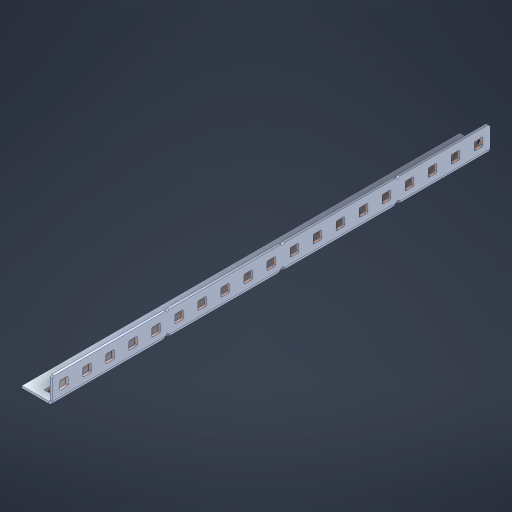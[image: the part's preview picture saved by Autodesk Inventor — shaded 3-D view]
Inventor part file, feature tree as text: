
AUTODESK INVENTOR PART (.ipt)
format: ipt  version: 2023 (Build 270158000, 158)  size: 732,672 bytes
history: native  units: in
note: dims shown in document units (in); Inventor stores cm internally (conversion verified against a paired STEP export)
features: other x43, extrude x37, sheet_metal_op x10, sketch x8, mirror x1, pattern_linear x1, chamfer x1
ambient origin geometry x8: Origin, YZ Plane, XZ Plane, XY Plane, X Axis, Y Axis, Z Axis, Center Point
bodies: Solid1 (feature_tree), Body (feature_tree)
feature tree (101):
  other  "Flange Pattern Plane"
  sheet_metal_op  "Flange Pattern"
  sheet_metal_op  "Body Pattern"
  other  "Arc Length"
  mirror  "Notch Mirror"
  pattern_linear  "Notch Pattern"  Spacing1=0.1875in  [1 undecoded]
  chamfer  "End Chamfer"
  extrude  "Half Cut"  Depth=0.0469in
  sketch  "Sketch1"  dims[d0=2.5in]
  other  "Plate1"
  sketch  "Sketch2"  dims[d1=9.5in]
  other  "Plate2"
  sheet_metal_op  "Bend1"
  sheet_metal_op  "Corner1"
  sketch  "Sketch3"  dims[d2=0.0469in]
  other  "Flange Pattern Sketch"
  sketch  "Sketch7"  dims[d3=0.0469in]
  other  "Srf1"
  other  "Srf2"
  sketch  "Sketch8"  dims[d4=0.0234in]
  sketch  "Sketch9"  dims[d5=0.0938in]
  other  "Srf91"
  sheet_metal_op  "Body Pattern Sketch"
  other  "Srf92"
  sketch  "Sketch13"  dims[d6=0.0469in]
  sketch  "Sketch14"  dims[d7=0.5in d8=90.0deg d9=0.0312in d10=0.1875in d11=0.0469in d12=0.0469in d16=0.182in d17=0.02in d18=0.0469in d19=0.0in d20=0.25in d21=0.25in d46=0.172in d47=1.0in d48=0.0in d49=0.182in d50=0.02in d51=0.25in d52=0.25in d53=0.0469in d54=0.0in d55=0.172in d56=1.0in d57=0.0in d60=7.4803in d62=0.5in d63=0.3937in d65=0.5in d85=0.1227in d86=0.1659in d88=0.04in d89=0.0469in d90=0.0in d91=0.04in d92=0.0491in d95=2.5in d96=0.04in d97=0.25in d98=45.0deg d101=0.0in d102=2.497in d131=0.5in d132=7.4803in d134=0.5in d139=0.5in]
  other  "Srf856"
  other  "Srf1310"
  other  "Srf1311"
  other  "Srf1312"
  other  "Srf1376"
  other  "Srf1377"
  other  "Srf1728"
  other  "Srf1755"
  other  "Srf1878"
  other  "Srf1879"
  other  "Srf1880"
  other  "Srf1881"
  other  "Srf1882"
  other  "Srf1883"
  other  "Srf1884"
  other  "Srf1885"
  other  "Srf1886"
  other  "Srf1887"
  other  "Srf1888"
  other  "Srf1889"
  other  "Srf1890"
  other  "Srf1942"
  other  "Srf1943"
  other  "Srf1944"
  other  "Srf1945"
  other  "Srf1946"
  other  "Srf1947"
  other  "Srf1948"
  other  "Srf1949"
  other  "Srf1950"
  other  "Srf1951"
  other  "Srf1952"
  other  "Srf1953"
  other  "Srf1954"
  sheet_metal_op  "Flange Stamp"
  sheet_metal_op  "Flange Circle"
  sheet_metal_op  "Body Stamp"
  sheet_metal_op  "Body Circle"
  sheet_metal_op  "Notch"
  extrude  "ExtrusionSrf2"  Depth=0.0469in
  extrude  "ExtrusionSrf92"  Depth=0.5in
  extrude  "ExtrusionSrf856"  Depth=0.02in
  extrude  "ExtrusionSrf1310"  Depth=0.0469in
  extrude  "ExtrusionSrf1311"  TaperAngle=0.0deg  [1 undecoded]
  extrude  "ExtrusionSrf1312"  Depth=0.5in
  extrude  "ExtrusionSrf1376"  Depth=0.5in
  extrude  "ExtrusionSrf1377"  Depth=0.5in
  extrude  "ExtrusionSrf1728"  Depth=0.5in TaperAngle=0.0deg
  extrude  "ExtrusionSrf1755"  Depth=0.5in
  extrude  "ExtrusionSrf1878"  Depth=0.02in
  extrude  "ExtrusionSrf1879"  Depth=0.5in
  extrude  "ExtrusionSrf1880"  Depth=0.5in
  extrude  "ExtrusionSrf1881"  Depth=0.0469in
  extrude  "ExtrusionSrf1882"  TaperAngle=0.0deg  [1 undecoded]
  extrude  "ExtrusionSrf1883"  Depth=0.5in
  extrude  "ExtrusionSrf1884"  Depth=0.5in TaperAngle=0.0deg
  extrude  "ExtrusionSrf1885"  Depth=0.5in
  extrude  "ExtrusionSrf1886"  Depth=0.5in
  extrude  "ExtrusionSrf1887"  Depth=0.5in
  extrude  "ExtrusionSrf1888"  Depth=0.5in
  extrude  "ExtrusionSrf1889"  Depth=0.5in
  extrude  "ExtrusionSrf1890"  Depth=0.0469in
  extrude  "ExtrusionSrf1942"  TaperAngle=0.0deg  [1 undecoded]
  extrude  "ExtrusionSrf1943"  Depth=0.5in
  extrude  "ExtrusionSrf1944"  Depth=0.5in
  extrude  "ExtrusionSrf1945"  Depth=0.5in
  extrude  "ExtrusionSrf1946"  Depth=0.5in TaperAngle=45.0deg
  extrude  "ExtrusionSrf1947"  TaperAngle=0.0deg  [1 undecoded]
  extrude  "ExtrusionSrf1948"  Depth=0.5in
  extrude  "ExtrusionSrf1949"  Depth=0.5in
  extrude  "ExtrusionSrf1950"  Depth=0.5in
  extrude  "ExtrusionSrf1951"  Depth=0.5in
  extrude  "ExtrusionSrf1952"  Depth=0.5in
  extrude  "ExtrusionSrf1953"  [1 undecoded]
  extrude  "ExtrusionSrf1954"  [1 undecoded]
note: 7 required parameter values undecoded (feature->parameter linkage not recoverable at this tier; creation-order binding heuristic only, values carry confidence <= 0.55)
